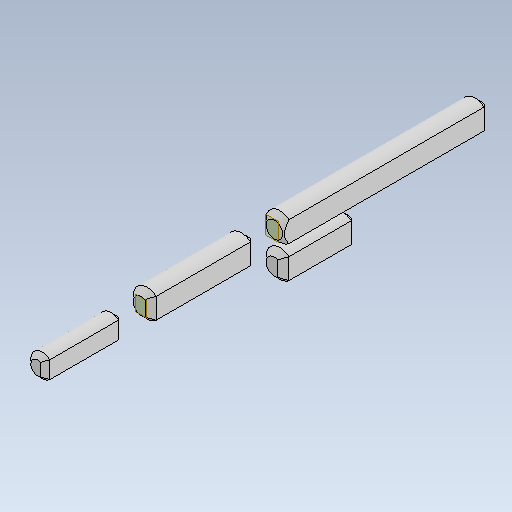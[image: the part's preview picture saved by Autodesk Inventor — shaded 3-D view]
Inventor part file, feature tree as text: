
AUTODESK INVENTOR PART (.ipt)
format: ipt  version: 2023 (Build 270158030, 158C)  size: 203,776 bytes
history: native  units: mm
features: projected_geometry x10, other x4, extrude x4, sketch x4, chamfer x3, plane x2
ambient origin geometry x8: Origin, YZ Plane, XZ Plane, XY Plane, X Axis, Y Axis, Z Axis, Center Point
bodies: Body1 (feature_tree), Body2 (feature_tree), Body3 (feature_tree), Body4 (feature_tree)
feature tree (27):
  other  "5x17mm"
  extrude  "Extrusion1"  Depth=26.0mm
  chamfer  "Chamfer1"  Distance=5.0mm
  plane  "Work Plane1"
  extrude  "Extrusion2"  Depth=5.0mm
  chamfer  "Chamfer2"  Distance=6.0mm
  plane  "Work Plane2"
  extrude  "Extrusion3"  Depth=6.0mm
  extrude  "Extrusion4"  Depth=2.0mm TaperAngle=0.0deg
  chamfer  "Chamfer3"  Distance=2.0mm Angle=45.0deg
  sketch  "Sketch1"  dims[d0=5.0mm d1=26.0mm]
  sketch  "Sketch2"  dims[d2=1.65mm d3=5.0mm d4=1.65mm]
  sketch  "Sketch3"  dims[d5=5.0mm d6=1.65mm d7=5.0mm d8=1.65mm]
  projected_geometry  "Projected Loop1"
  projected_geometry  "Projected Loop2"
  projected_geometry  "Projected Loop3"
  projected_geometry  "Projected Loop4"
  sketch  "Sketch4"  dims[d9=6.0mm d10=6.0mm d11=6.0mm d12=17.0mm d13=0.0mm d14=1.0mm d15=2.0mm d16=45.0deg d17=6.0mm d18=6.0mm d19=1.98mm d20=6.0mm d21=1.98mm d22=7.0mm d23=6.0mm d24=1.98mm d25=6.0mm d26=1.98mm d27=7.0mm d28=7.0mm d29=23.0mm d30=0.0mm d31=1.2mm d32=2.0mm d33=45.0deg d34=6.0mm d35=45.0mm d36=0.0mm d37=16.0mm d38=0.0mm d39=1.2mm d40=2.0mm d41=45.0deg]
  projected_geometry  "Projected Loop5"
  projected_geometry  "Projected Loop6"
  projected_geometry  "Projected Loop7"
  projected_geometry  "Projected Loop8"
  projected_geometry  "Projected Loop9"
  projected_geometry  "Projected Loop10"
  other  "6x23mm"
  other  "6x16mm"
  other  "6x45mm"
